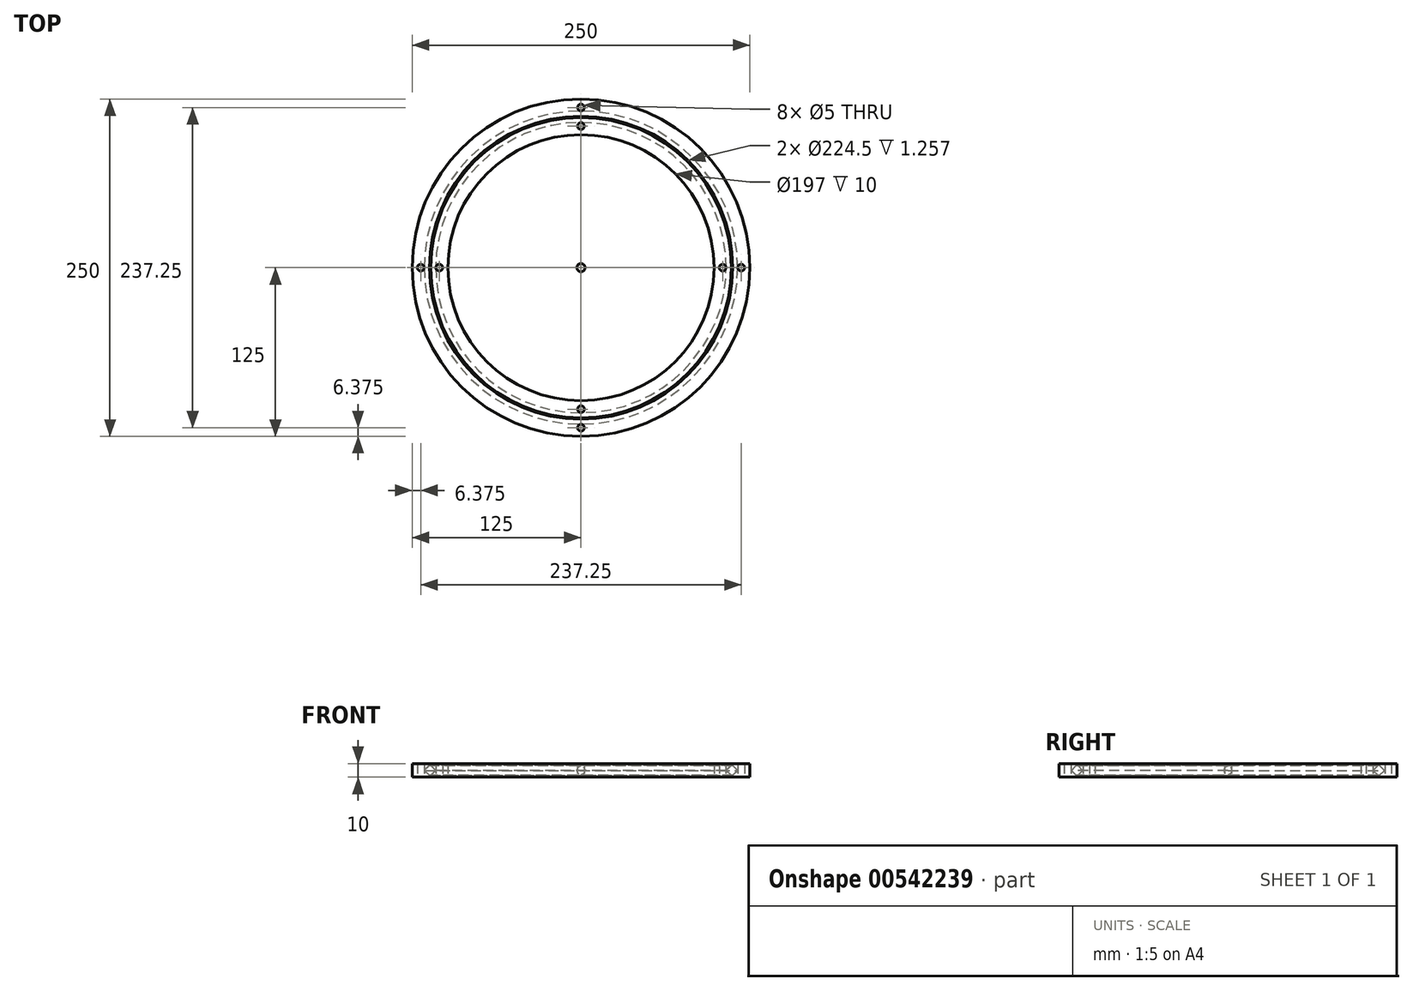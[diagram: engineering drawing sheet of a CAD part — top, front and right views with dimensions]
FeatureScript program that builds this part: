
annotation { "Feature Type Name" : "Feature", "Feature Type Description" : "" }
export const myFeature = defineFeature(function(context is Context, id is Id, definition is map)
    precondition{}
    {
        {
            assignVariable(context, id + "F0", {"name" : "h", "anyValue" : 10});
        }
        {
            var Q0;
            Q0=qCreatedBy(makeId("Top.planeOp"),FACE);
            var sketch = newSketch(context, id + "F1", { "sketchPlane" : qUnion([Q0])});
            skCircle(sketch, "E0", {"center": v(0, 0) * mm, "radius": 125 * mm});
            skCircle(sketch, "E1", {"center": v(0, 0) * mm, "radius": 112.25 * mm});
            skLineSegment(sketch, "E2", {"start": v(0, 108.79) * mm, "end": v(0, -107.46) * mm, "construction": true});
            skLineSegment(sketch, "E3", {"start": v(-112.1, 0) * mm, "end": v(109.19, 0) * mm, "construction": true});
            skCircle(sketch, "E4", {"center": v(0, 0) * mm, "radius": 118.63 * mm, "construction": true});
            skCircle(sketch, "E5", {"center": v(0, 118.63) * mm, "radius": 2.5 * mm});
            skCircle(sketch, "E6.1.0", {"center": v(-118.63, 0) * mm, "radius": 2.5 * mm});
            skCircle(sketch, "E6.2.0", {"center": v(0, -118.63) * mm, "radius": 2.5 * mm});
            skCircle(sketch, "E7.1.3.0", {"center": v(118.63, 0) * mm, "radius": 2.5 * mm});
            skSolve(sketch);
        }
        {
            var Q0;
            Q0=qSketchRegion(id+"F1",true);
            extrude(context, id + "F2", {"entities" : qUnion([Q0]), "endBound" : BoundingType.SYMMETRIC, "depth" : (getVariable(context, 'h')) * mm, "offsetDistance" : 25 * mm});
        }
        {
            var Q0;
            Q0=qCreatedBy(makeId("Top.planeOp"),FACE);
            var sketch = newSketch(context, id + "F3", { "sketchPlane" : qUnion([Q0])});
            skCircle(sketch, "E8", {"center": v(0, 0) * mm, "radius": 111.25 * mm});
            skCircle(sketch, "E9", {"center": v(0, 0) * mm, "radius": 98.5 * mm});
            skCircle(sketch, "E10", {"center": v(0, 0) * mm, "radius": 104.88 * mm, "construction": true});
            skCircle(sketch, "E11", {"center": v(0, 104.88) * mm, "radius": 2.5 * mm});
            skCircle(sketch, "E12.1.0", {"center": v(-104.88, 0) * mm, "radius": 2.5 * mm});
            skCircle(sketch, "E12.2.0", {"center": v(0, -104.88) * mm, "radius": 2.5 * mm});
            skCircle(sketch, "E13.1.3.0", {"center": v(104.88, 0) * mm, "radius": 2.5 * mm});
            skSolve(sketch);
        }
        {
            var Q0;
            Q0=qSketchRegion(id+"F3",true);
            extrude(context, id + "F4", {"entities" : qUnion([Q0]), "endBound" : BoundingType.SYMMETRIC, "depth" : (getVariable(context, 'h')) * mm, "offsetDistance" : 25 * mm});
        }
        {
            var Q0;
            Q0=qCreatedBy(makeId("Front.planeOp"),FACE);
            var sketch = newSketch(context, id + "F5", { "sketchPlane" : qUnion([Q0])});
            skCircle(sketch, "E14", {"center": v(111.75, 0) * mm, "radius": 3 * mm, "construction": true});
            skLineSegment(sketch, "E15", {"start": v(111.75, 4.24) * mm, "end": v(107.5, 0) * mm});
            skLineSegment(sketch, "E16", {"start": v(107.5, 0) * mm, "end": v(111.75, -4.24) * mm});
            skLineSegment(sketch, "E17", {"start": v(111.75, 4.24) * mm, "end": v(116, 0) * mm});
            skLineSegment(sketch, "E18", {"start": v(116, 0) * mm, "end": v(111.75, -4.24) * mm});
            skSolve(sketch);
        }
        {
            var Q0;
            Q0=qSketchRegion(id+"F5",true);
            var Q1;
            Q1=makeQuery(id+"F4.opExtrude","SWEPT_FACE",FACE,{"disambiguationData":[OSD([sQuery(id+"F3.wireOp",EDGE,"E9")])]});
            revolve(context, id + "F6", {"entities" : qUnion([Q0]), "axis" : qUnion([Q1]), "revolveType" : RevolveType.FULL});
        }
        {
            var Q0;
            Q0=makeQuery(id+"F6.opRevolve","SWEPT_BODY",BODY,{"disambiguationData":[OSD([sQuery(id+"F5.wireOp",EDGE,"E15"),sQuery(id+"F5.wireOp",EDGE,"E16"),sQuery(id+"F5.wireOp",EDGE,"E17"),sQuery(id+"F5.wireOp",EDGE,"E18")])]});
            var Q1;
            Q1=makeQuery(id+"F2.opExtrude","SWEPT_BODY",BODY,{"disambiguationData":[OSD([sQuery(id+"F1.wireOp",EDGE,"E0"),sQuery(id+"F1.wireOp",EDGE,"E1"),sQuery(id+"F1.wireOp",EDGE,"E5"),sQuery(id+"F1.wireOp",EDGE,"E6.1.0"),sQuery(id+"F1.wireOp",EDGE,"E6.2.0"),sQuery(id+"F1.wireOp",EDGE,"E7.1.3.0")])]});
            var Q2;
            Q2=makeQuery(id+"F4.opExtrude","SWEPT_BODY",BODY,{"disambiguationData":[OSD([sQuery(id+"F3.wireOp",EDGE,"E8"),sQuery(id+"F3.wireOp",EDGE,"E9"),sQuery(id+"F3.wireOp",EDGE,"E11"),sQuery(id+"F3.wireOp",EDGE,"E12.1.0"),sQuery(id+"F3.wireOp",EDGE,"E12.2.0"),sQuery(id+"F3.wireOp",EDGE,"E13.1.3.0")])]});
            booleanBodies(context, id + "F7", {"operationType" : BooleanOperationType.SUBTRACTION, "tools" : qUnion([Q0]), "targets" : qUnion([Q1, Q2])});
        }
        {
            var Q0;
            Q0=qCreatedBy(makeId("Front.planeOp"),FACE);
            var sketch = newSketch(context, id + "F8", { "sketchPlane" : qUnion([Q0])});
            skArc(sketch, "E19", {"start": v(0, -3) * mm, "mid": v(3, 0) * mm, "end": v(0, 3) * mm});
            skLineSegment(sketch, "E20", {"start": v(0, 3) * mm, "end": v(0, -3) * mm});
            skSolve(sketch);
        }
        {
            var Q0;
            Q0=qSketchRegion(id+"F8",true);
            var Q1;
            Q1=sQuery(id+"F8.wireOp",EDGE,"E20");
            revolve(context, id + "F9", {"entities" : qUnion([Q0]), "axis" : qUnion([Q1]), "revolveType" : RevolveType.FULL});
        }
    });
